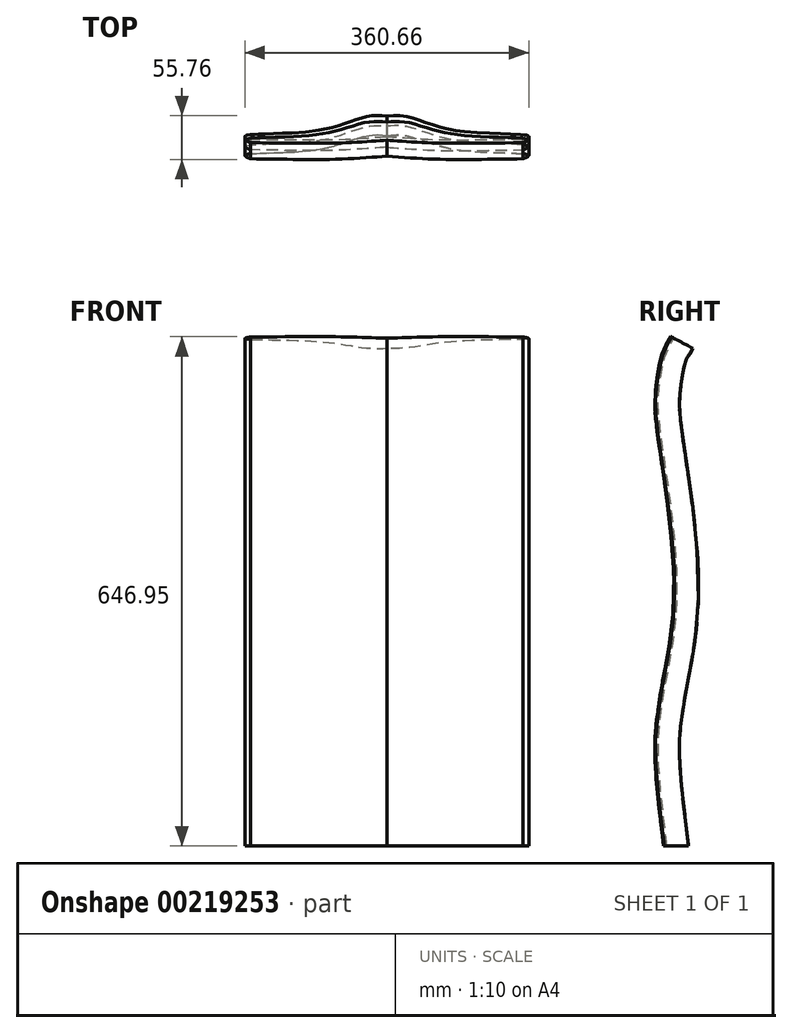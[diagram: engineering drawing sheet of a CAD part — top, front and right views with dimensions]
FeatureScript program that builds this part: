
annotation { "Feature Type Name" : "Feature", "Feature Type Description" : "" }
export const myFeature = defineFeature(function(context is Context, id is Id, definition is map)
    precondition{}
    {
        {
            var Q0;
            Q0=qCreatedBy(makeId("Front.planeOp"),FACE);
            var sketch = newSketch(context, id + "F0", { "sketchPlane" : qUnion([Q0])});
            skLineSegment(sketch, "E0.bottom", {"start": v(0, 635) * mm, "end": v(254, 635) * mm, "construction": true});
            skLineSegment(sketch, "E0.top", {"start": v(0, 0) * mm, "end": v(254, 0) * mm, "construction": true});
            skLineSegment(sketch, "E0.left", {"start": v(0, 635) * mm, "end": v(0, 0) * mm, "construction": true});
            skLineSegment(sketch, "E0.right", {"start": v(254, 635) * mm, "end": v(254, 0) * mm, "construction": true});
            skPoint(sketch, "E1.3.internal.snap0", {"position": v(127, 635) * mm});
            skFitSpline(sketch, "E2", {"points": [v(0, 635) * mm, v(23.76, 635) * mm, v(83.6, 640.98) * mm, v(154.77, 645.83) * mm, v(208.15, 639.9) * mm, v(234.03, 624.8) * mm, v(245.35, 598.39) * mm, v(242.11, 562.8) * mm, v(225.4, 501.34) * mm, v(206.53, 429.1) * mm, v(196.82, 357.39) * mm, v(178.66, 235.4) * mm, v(173.05, 89.6) * mm, v(169.31, 39.13) * mm, v(135.66, 24.17) * mm, v(72.1, 0) * mm, v(0, 0) * mm], "startDerivative": vector(533.92, -19.43) * mm, "endDerivative": vector(-1064.93, 113.04) * mm});
            skFitSpline(sketch, "E3.MirrorCS", {"points": [v(0, 635) * mm, v(-23.76, 635) * mm, v(-83.6, 640.98) * mm, v(-154.77, 645.83) * mm, v(-208.15, 639.9) * mm, v(-234.03, 624.8) * mm, v(-245.35, 598.39) * mm, v(-242.11, 562.8) * mm, v(-225.4, 501.34) * mm, v(-206.53, 429.1) * mm, v(-196.82, 357.39) * mm, v(-178.66, 235.4) * mm, v(-173.05, 89.6) * mm, v(-169.31, 39.13) * mm, v(-135.66, 24.17) * mm, v(-72.1, 0) * mm, v(0, 0) * mm], "startDerivative": vector(-533.92, -19.43) * mm, "endDerivative": vector(1064.93, 113.04) * mm});
            skSolve(sketch);
        }
        {
            var Q0;
            Q0=qCreatedBy(makeId("Right.planeOp"),FACE);
            var sketch = newSketch(context, id + "F1", { "sketchPlane" : qUnion([Q0])});
            skFitSpline(sketch, "E4", {"points": [v(171.06, 645.13) * mm, v(162.22, 629.51) * mm, v(152.04, 580.59) * mm, v(152.04, 541.07) * mm, v(171.06, 400.34) * mm, v(171.06, 266.51) * mm, v(151.5, 141.95) * mm, v(162.22, 0) * mm], "startDerivative": vector(-79.45, -199.07) * mm, "endDerivative": vector(99.4, -853.12) * mm});
            skSolve(sketch);
        }
        {
            var Q0;
            Q0=qCreatedBy(makeId("Top.planeOp"),FACE);
            var sketch = newSketch(context, id + "F2", { "sketchPlane" : qUnion([Q0])});
            skFitSpline(sketch, "E5", {"points": [v(0, 162.75) * mm, v(52.6, 159.23) * mm, v(173.07, 159.35) * mm], "startDerivative": vector(84.15, -5.7) * mm, "endDerivative": vector(284.64, 4.49) * mm});
            skFitSpline(sketch, "E6.MirrorCS", {"points": [v(0, 162.75) * mm, v(52.6, 159.23) * mm, v(173.07, 159.35) * mm], "startDerivative": vector(84.15, -5.7) * mm, "endDerivative": vector(284.64, 4.49) * mm});
            skFitSpline(sketch, "E7.MirrorCS", {"points": [v(0, 162.75) * mm, v(-52.6, 159.23) * mm, v(-173.07, 159.35) * mm], "startDerivative": vector(-84.15, -5.7) * mm, "endDerivative": vector(-284.64, 4.49) * mm});
            skFitSpline(sketch, "E8", {"points": [v(173.07, 159.35) * mm, v(180.28, 163.72) * mm, v(121.57, 167.88) * mm, v(63.4, 176.71) * mm, v(22.87, 189.18) * mm, v(0, 189.18) * mm], "startDerivative": vector(118.63, 49.14) * mm, "endDerivative": vector(-132.12, -13.73) * mm});
            skFitSpline(sketch, "E9.MirrorCS", {"points": [v(-173.07, 159.35) * mm, v(-180.28, 163.72) * mm, v(-121.57, 167.88) * mm, v(-63.4, 176.71) * mm, v(-22.87, 189.18) * mm, v(0, 189.18) * mm], "startDerivative": vector(-118.63, 49.14) * mm, "endDerivative": vector(132.12, -13.73) * mm});
            skSolve(sketch);
        }
        {
            var Q0;
            Q0=qCreatedBy(makeId("Top.planeOp"),FACE);
            var Q1;
            Q1=sQuery(id+"F1.wireOp",VERTEX,"E4.6.internal");
            cPlane(context, id + "F3", {"entities" : qUnion([Q0, Q1]), "cplaneType" : CPlaneType.PLANE_POINT, "offset" : 25.4 * mm, "width" : 152.4 * mm, "height" : 152.4 * mm});
        }
        {
            var Q0;
            Q0=sQuery(id+"F1.wireOp",VERTEX,"E4.5.internal");
            var Q1;
            Q1=qCreatedBy(id+"F3.planeOp",FACE);
            cPlane(context, id + "F4", {"entities" : qUnion([Q0, Q1]), "cplaneType" : CPlaneType.PLANE_POINT, "offset" : 25.4 * mm, "width" : 152.4 * mm, "height" : 152.4 * mm});
        }
        {
            var Q0;
            Q0=qCreatedBy(id+"F4.planeOp",FACE);
            var Q1;
            Q1=sQuery(id+"F1.wireOp",VERTEX,"E4.4.internal");
            cPlane(context, id + "F5", {"entities" : qUnion([Q0, Q1]), "cplaneType" : CPlaneType.PLANE_POINT, "offset" : 25.4 * mm, "width" : 152.4 * mm, "height" : 152.4 * mm});
        }
        {
            var Q0;
            Q0 = qSketchRegion(id + "F2", true);
            var Q1;
            Q1=sQuery(id+"F1.wireOp",EDGE,"E4");
            sweep(context, id + "F6", {"profiles" : qUnion([Q0]), "path" : qUnion([Q1])});
        }
    });
